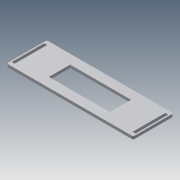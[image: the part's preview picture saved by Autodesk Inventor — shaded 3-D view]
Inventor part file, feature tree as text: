
AUTODESK INVENTOR PART (.ipt)
format: ipt  version: 2014 (Build 180170000, 170)  size: 113,664 bytes
history: native  units: mm
features: extrude x3, sketch x3, fillet x1
ambient origin geometry x8: Origin, YZ Plane, XZ Plane, XY Plane, X Axis, Y Axis, Z Axis, Center Point
bodies: Solid1 (feature_tree)
feature tree (7):
  extrude  "Extrusion1"  Depth=268.0mm
  extrude  "Extrusion2"  Depth=2.875mm
  fillet  "Fillet1"  Radius=6.25mm
  extrude  "Extrusion5"  Depth=20.0mm TaperAngle=0.0deg
  sketch  "Sketch1"  dims[d0=85.0mm d1=268.0mm]
  sketch  "Sketch2"  dims[d2=6.0mm d3=0.0mm d5=2.875mm d6=6.25mm]
  sketch  "Sketch4"  dims[d8=8.0mm d9=4.0mm d10=0.0mm d11=3.0mm d30=10.0mm d31=0.0mm d33=20.0mm d34=2.875mm d35=8.0mm d36=129.0mm d37=20.0mm]
